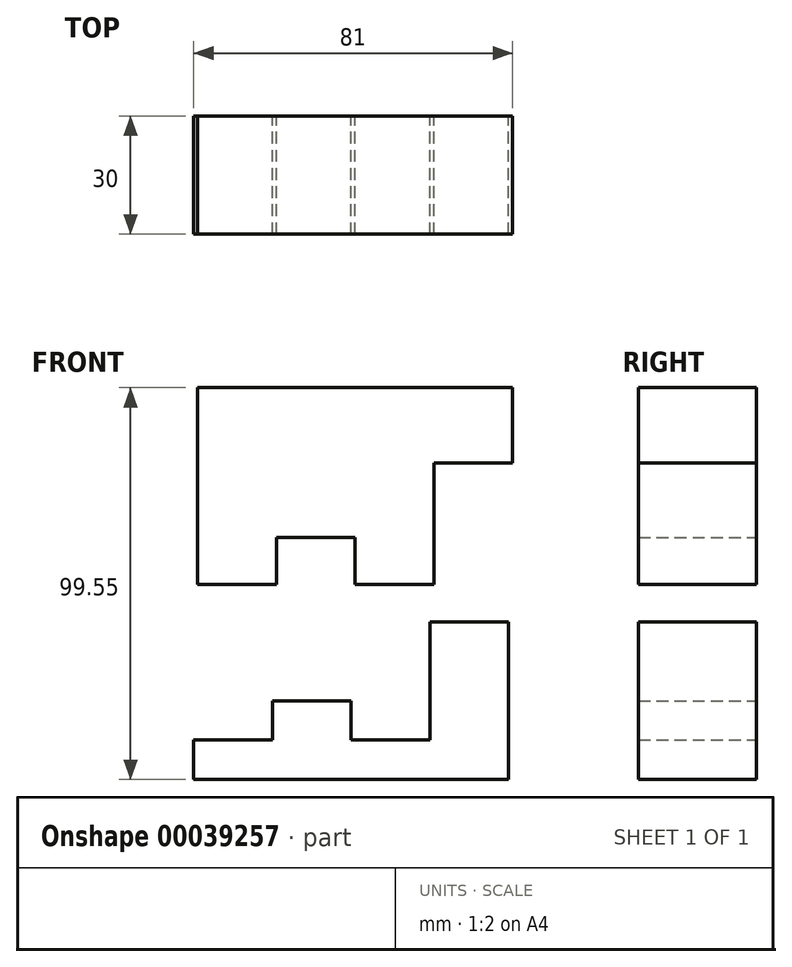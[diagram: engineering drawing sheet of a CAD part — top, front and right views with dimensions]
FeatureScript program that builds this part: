
annotation { "Feature Type Name" : "Feature", "Feature Type Description" : "" }
export const myFeature = defineFeature(function(context is Context, id is Id, definition is map)
    precondition{}
    {
        {
            var Q0;
            Q0=qCreatedBy(makeId("Front.planeOp"),FACE);
            var sketch = newSketch(context, id + "F0", { "sketchPlane" : qUnion([Q0])});
            skLineSegment(sketch, "E0.bottom", {"start": v(-47.64, 50) * mm, "end": v(32.36, 50) * mm});
            skLineSegment(sketch, "E0.top", {"start": v(-47.64, 0) * mm, "end": v(-27.64, 0) * mm});
            skLineSegment(sketch, "E0.left", {"start": v(-47.64, 50) * mm, "end": v(-47.64, 0) * mm});
            skLineSegment(sketch, "E0.right", {"start": v(32.36, 50) * mm, "end": v(32.36, 30.8) * mm});
            skLineSegment(sketch, "E1", {"start": v(-27.64, 0) * mm, "end": v(-27.64, 11.93) * mm});
            skLineSegment(sketch, "E2", {"start": v(-27.64, 11.93) * mm, "end": v(-7.64, 11.93) * mm});
            skLineSegment(sketch, "E3", {"start": v(-7.64, 11.93) * mm, "end": v(-7.64, 0) * mm});
            skLineSegment(sketch, "E4", {"start": v(-7.64, 0) * mm, "end": v(12.36, 0) * mm});
            skLineSegment(sketch, "E5", {"start": v(12.36, 0) * mm, "end": v(12.36, 30.8) * mm});
            skLineSegment(sketch, "E6", {"start": v(12.36, 30.8) * mm, "end": v(32.36, 30.8) * mm});
            skPoint(sketch, "E7.orphan", {"position": v(32.36, 0) * mm});
            skSolve(sketch);
        }
        {
            var Q0;
            Q0=makeQuery(id+"F0.imprint","IMPRINT",FACE,{"disambiguationData":[TD([[makeQuery(id+"F0.imprint","IMPRINT",EDGE,{"derivedFrom":sQuery(id+"F0.wireOp",EDGE,"E0.bottom")}),-1.0]])]});
            extrude(context, id + "F1", {"entities" : qUnion([Q0]), "depth" : 30 * mm});
        }
        {
            var Q0;
            Q0=qCreatedBy(makeId("Front.planeOp"),FACE);
            var sketch = newSketch(context, id + "F2", { "sketchPlane" : qUnion([Q0])});
            skLineSegment(sketch, "E8.bottom", {"start": v(11.36, -9.55) * mm, "end": v(31.36, -9.55) * mm});
            skLineSegment(sketch, "E8.top", {"start": v(-48.64, -49.55) * mm, "end": v(31.36, -49.55) * mm});
            skLineSegment(sketch, "E8.left", {"start": v(-48.64, -39.55) * mm, "end": v(-48.64, -49.55) * mm});
            skLineSegment(sketch, "E8.right", {"start": v(31.36, -9.55) * mm, "end": v(31.36, -49.55) * mm});
            skLineSegment(sketch, "E9", {"start": v(-48.64, -39.55) * mm, "end": v(-28.64, -39.55) * mm});
            skLineSegment(sketch, "E10", {"start": v(-28.64, -39.55) * mm, "end": v(-28.64, -29.55) * mm});
            skLineSegment(sketch, "E11", {"start": v(-28.64, -29.55) * mm, "end": v(-8.64, -29.55) * mm});
            skLineSegment(sketch, "E12", {"start": v(-8.64, -29.55) * mm, "end": v(-8.64, -39.55) * mm});
            skLineSegment(sketch, "E13", {"start": v(-8.64, -39.55) * mm, "end": v(11.36, -39.55) * mm});
            skLineSegment(sketch, "E14", {"start": v(11.36, -39.55) * mm, "end": v(11.36, -9.55) * mm});
            skSolve(sketch);
        }
        {
            var Q0;
            Q0=makeQuery(id+"F2.imprint","IMPRINT",FACE,{"disambiguationData":[TD([[makeQuery(id+"F2.imprint","IMPRINT",EDGE,{"derivedFrom":sQuery(id+"F2.wireOp",EDGE,"E8.bottom")}),-1.0]])]});
            extrude(context, id + "F3", {"entities" : qUnion([Q0]), "depth" : 30 * mm});
        }
    });
